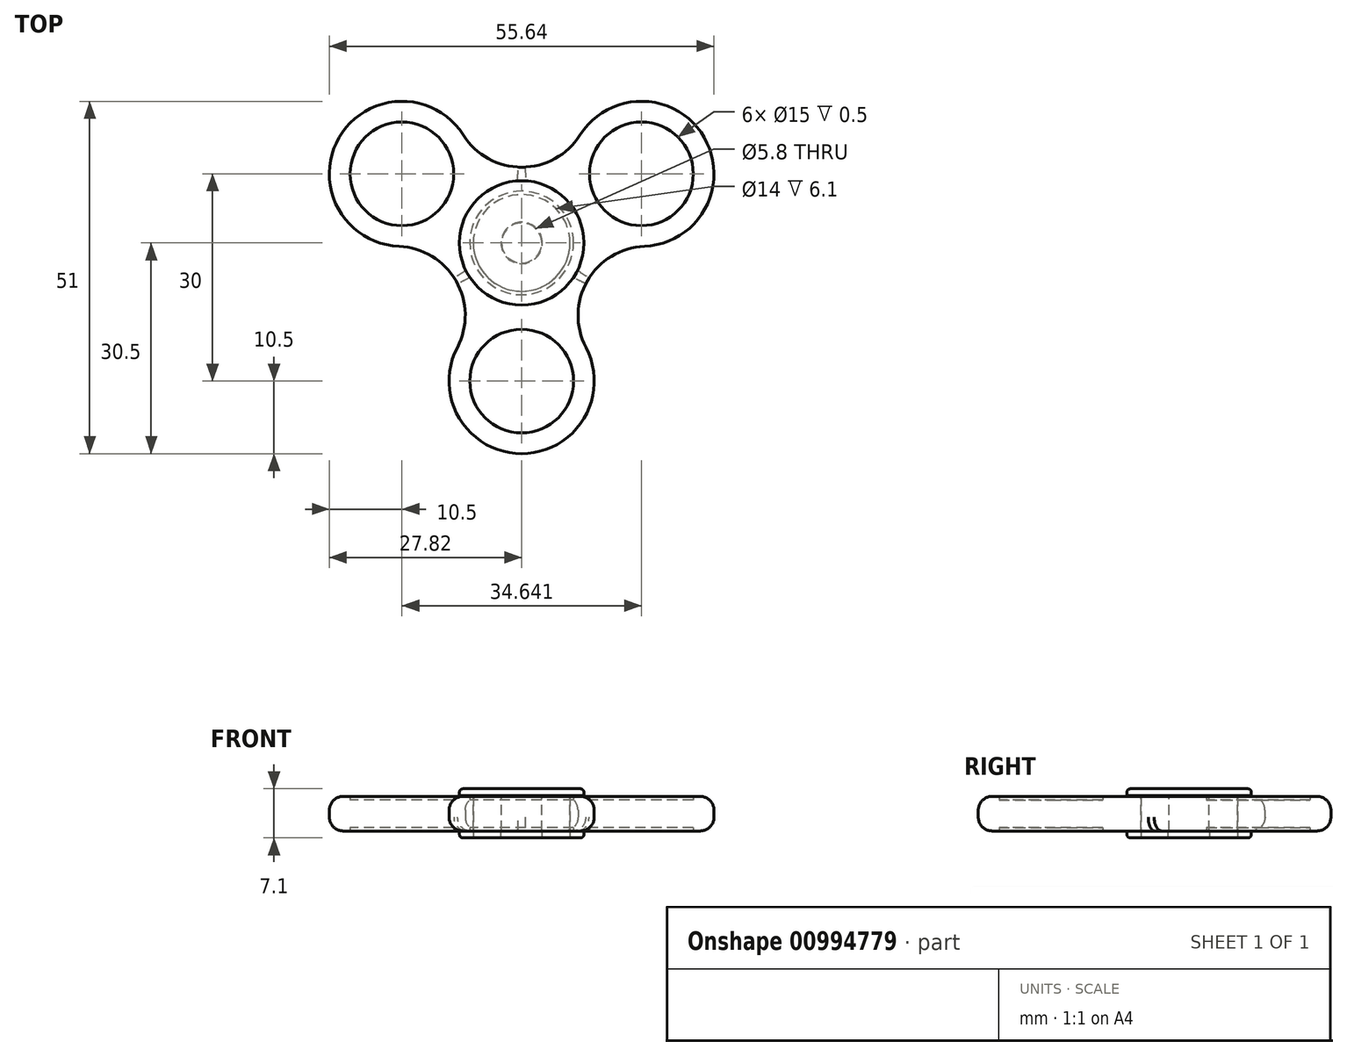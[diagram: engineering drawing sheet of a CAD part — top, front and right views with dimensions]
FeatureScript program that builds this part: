
annotation { "Feature Type Name" : "Feature", "Feature Type Description" : "" }
export const myFeature = defineFeature(function(context is Context, id is Id, definition is map)
    precondition{}
    {
        {
            var Q0;
            Q0=qCreatedBy(makeId("Top.planeOp"),FACE);
            var sketch = newSketch(context, id + "F0", { "sketchPlane" : qUnion([Q0])});
            skCircle(sketch, "E0", {"center": v(0, 0) * mm, "radius": 7.5 * mm});
            skCircle(sketch, "E1", {"center": v(0, -20) * mm, "radius": 7.5 * mm});
            skArc(sketch, "E2", {"start": v(-9.3, -15.13) * mm, "mid": v(0, -30.5) * mm, "end": v(9.3, -15.13) * mm});
            skArc(sketch, "E3.1.0", {"start": v(17.75, -0.5) * mm, "mid": v(26.41, 15.25) * mm, "end": v(8.45, 15.62) * mm});
            skCircle(sketch, "E3.1.1", {"center": v(17.32, 10) * mm, "radius": 7.5 * mm});
            skArc(sketch, "E3.2.0", {"start": v(-8.45, 15.62) * mm, "mid": v(-26.41, 15.25) * mm, "end": v(-17.75, -0.5) * mm});
            skCircle(sketch, "E3.2.1", {"center": v(-17.32, 10) * mm, "radius": 7.5 * mm});
            skArc(sketch, "E4", {"start": v(-9.3, -15.13) * mm, "mid": v(-9.5, -5.48) * mm, "end": v(-17.75, -0.5) * mm});
            skArc(sketch, "E5.1.0", {"start": v(17.75, -0.5) * mm, "mid": v(9.5, -5.48) * mm, "end": v(9.3, -15.13) * mm});
            skArc(sketch, "E5.2.0", {"start": v(-8.45, 15.62) * mm, "mid": v(0, 10.97) * mm, "end": v(8.45, 15.62) * mm});
            skSolve(sketch);
        }
        {
            var Q0;
            Q0=makeQuery(id+"F0.imprint","IMPRINT",FACE,{"disambiguationData":[TD([[makeQuery(id+"F0.imprint","IMPRINT",EDGE,{"derivedFrom":sQuery(id+"F0.wireOp",EDGE,"E0")}),-1.0]])]});
            extrude(context, id + "F1", {"entities" : qUnion([Q0]), "endBound" : BoundingType.SYMMETRIC, "depth" : 5 * mm, "offsetDistance" : 25 * mm});
        }
        {
            var Q0;
            Q0=makeQuery(id+"F0.imprint","IMPRINT",FACE,{"disambiguationData":[TD([[makeQuery(id+"F0.imprint","IMPRINT",EDGE,{"derivedFrom":sQuery(id+"F0.wireOp",EDGE,"E3.1.1")}),1.0]])]});
            var Q1;
            Q1=makeQuery(id+"F0.imprint","IMPRINT",FACE,{"disambiguationData":[TD([[makeQuery(id+"F0.imprint","IMPRINT",EDGE,{"derivedFrom":sQuery(id+"F0.wireOp",EDGE,"E3.2.1")}),1.0]])]});
            var Q2;
            Q2=makeQuery(id+"F0.imprint","IMPRINT",FACE,{"disambiguationData":[TD([[makeQuery(id+"F0.imprint","IMPRINT",EDGE,{"derivedFrom":sQuery(id+"F0.wireOp",EDGE,"E1")}),1.0]])]});
            extrude(context, id + "F2", {"entities" : qUnion([Q0, Q1, Q2]), "operationType" : NewBodyOperationType.ADD, "endBound" : BoundingType.SYMMETRIC, "depth" : 4 * mm, "offsetDistance" : 25 * mm});
        }
        {
            var Q0;
            Q0=makeQuery(id+"F1.opExtrude","CAP_FACE",FACE,{"disambiguationData":[OSD([sQuery(id+"F0.wireOp",EDGE,"E0"),sQuery(id+"F0.wireOp",EDGE,"E1"),sQuery(id+"F0.wireOp",EDGE,"E2"),sQuery(id+"F0.wireOp",EDGE,"E3.1.0"),sQuery(id+"F0.wireOp",EDGE,"E3.1.1"),sQuery(id+"F0.wireOp",EDGE,"E3.2.0"),sQuery(id+"F0.wireOp",EDGE,"E3.2.1"),sQuery(id+"F0.wireOp",EDGE,"E4"),sQuery(id+"F0.wireOp",EDGE,"E5.1.0"),sQuery(id+"F0.wireOp",EDGE,"E5.2.0")])],"isStart":true});
            var sketch = newSketch(context, id + "F3", { "sketchPlane" : qUnion([Q0])});
            skCircle(sketch, "E6.0", {"center": v(0, 0) * mm, "radius": 7 * mm});
            skCircle(sketch, "E7", {"center": v(0, 0) * mm, "radius": 3 * mm});
            skCircle(sketch, "E8.0", {"center": v(0, 0) * mm, "radius": 9 * mm});
            skSolve(sketch);
        }
        {
            var Q0;
            Q0=makeQuery(id+"F3.imprint","IMPRINT",FACE,{"disambiguationData":[TD([[makeQuery(id+"F3.imprint","IMPRINT",EDGE,{"derivedFrom":sQuery(id+"F3.wireOp",EDGE,"E6.0")}),-1.0]])]});
            extrude(context, id + "F4", {"entities" : qUnion([Q0]), "oppositeDirection" : true, "depth" : 5.1 * mm, "offsetDistance" : 25 * mm});
        }
        {
            var Q0;
            Q0 = qSketchRegion(id + "F3", true);
            var Q1;
            Q1=makeQuery(id+"F3.imprint","IMPRINT",FACE,{"disambiguationData":[TD([[makeQuery(id+"F3.imprint","IMPRINT",EDGE,{"derivedFrom":sQuery(id+"F3.wireOp",EDGE,"E6.0")}),-1.0]])]});
            var Q2;
            Q2=makeQuery(id+"F3.imprint","IMPRINT",FACE,{"disambiguationData":[TD([[makeQuery(id+"F3.imprint","IMPRINT",EDGE,{"derivedFrom":sQuery(id+"F3.wireOp",EDGE,"E7")}),1.0]])]});
            var Q3;
            Q3=sQuery(id+"F0.wireOp",EDGE,"E0");
            extrude(context, id + "F5", {"entities" : qUnion([Q0, Q1, Q2]), "operationType" : NewBodyOperationType.ADD, "surfaceOperationType" : NewSurfaceOperationType.ADD, "surfaceEntities" : qUnion([Q3]), "depth" : 1 * mm, "offsetDistance" : 25 * mm});
        }
        {
            var Q0;
            Q0=makeQuery(id+"F4.opExtrude","CAP_FACE",FACE,{"disambiguationData":[OSD([sQuery(id+"F3.wireOp",EDGE,"E6.0"),sQuery(id+"F3.wireOp",EDGE,"E7")])],"isStart":false});
            var sketch = newSketch(context, id + "F6", { "sketchPlane" : qUnion([Q0])});
            skCircle(sketch, "E9.0", {"center": v(0, 0) * mm, "radius": 2.9 * mm});
            skCircle(sketch, "E10.0", {"center": v(0, 0) * mm, "radius": 9 * mm});
            skSolve(sketch);
        }
        {
            var Q0;
            Q0=makeQuery(id+"F6.imprint","IMPRINT",FACE,{"disambiguationData":[TD([[makeQuery(id+"F6.imprint","IMPRINT",EDGE,{"derivedFrom":sQuery(id+"F6.wireOp",EDGE,"E9.0")}),-1.0]])]});
            var Q1;
            Q1=makeQuery(id+"F1.opExtrude","CAP_FACE",FACE,{"disambiguationData":[OSD([sQuery(id+"F0.wireOp",EDGE,"E0"),sQuery(id+"F0.wireOp",EDGE,"E1"),sQuery(id+"F0.wireOp",EDGE,"E2"),sQuery(id+"F0.wireOp",EDGE,"E3.1.0"),sQuery(id+"F0.wireOp",EDGE,"E3.1.1"),sQuery(id+"F0.wireOp",EDGE,"E3.2.0"),sQuery(id+"F0.wireOp",EDGE,"E3.2.1"),sQuery(id+"F0.wireOp",EDGE,"E4"),sQuery(id+"F0.wireOp",EDGE,"E5.1.0"),sQuery(id+"F0.wireOp",EDGE,"E5.2.0")])],"isStart":true});
            extrude(context, id + "F7", {"entities" : qUnion([Q0]), "endBound" : BoundingType.UP_TO_SURFACE, "oppositeDirection" : true, "depth" : 25 * mm, "endBoundEntityFace" : qUnion([Q1]), "offsetDistance" : 25 * mm});
        }
        {
            var Q0;
            Q0=makeQuery(id+"F6.imprint","IMPRINT",FACE,{"disambiguationData":[TD([[makeQuery(id+"F6.imprint","IMPRINT",EDGE,{"derivedFrom":sQuery(id+"F6.wireOp",EDGE,"E10.0")}),1.0]])]});
            var Q1;
            Q1=makeQuery(id+"F6.imprint","IMPRINT",FACE,{"disambiguationData":[TD([[makeQuery(id+"F6.imprint","IMPRINT",EDGE,{"derivedFrom":makeQuery(id+"F4.opExtrude","CAP_EDGE",EDGE,{"disambiguationData":[OSD([sQuery(id+"F3.wireOp",EDGE,"E6.0")])],"isStart":false})}),1.0]])]});
            var Q2;
            Q2=makeQuery(id+"F6.imprint","IMPRINT",FACE,{"disambiguationData":[TD([[makeQuery(id+"F6.imprint","IMPRINT",EDGE,{"derivedFrom":sQuery(id+"F6.wireOp",EDGE,"E9.0")}),-1.0]])]});
            var Q3;
            Q3=makeQuery(id+"F6.imprint","IMPRINT",FACE,{"disambiguationData":[TD([[makeQuery(id+"F6.imprint","IMPRINT",EDGE,{"derivedFrom":sQuery(id+"F6.wireOp",EDGE,"E9.0")}),1.0]])]});
            extrude(context, id + "F8", {"entities" : qUnion([Q0, Q1, Q2, Q3]), "depth" : 1 * mm, "offsetDistance" : 25 * mm});
        }
        {
            var Q0;
            Q0=makeQuery(id+"F1.opExtrude","CAP_EDGE",EDGE,{"disambiguationData":[OSD([sQuery(id+"F0.wireOp",EDGE,"E3.2.0")])],"isStart":false});
            var Q1;
            Q1=makeQuery(id+"F1.opExtrude","CAP_EDGE",EDGE,{"disambiguationData":[OSD([sQuery(id+"F0.wireOp",EDGE,"E3.2.0")])],"isStart":true});
            fillet(context, id + "F9", {"entities" : qUnion([Q0, Q1]), "radius" : 2 * mm, "tangentPropagation" : true, "allowEdgeOverflow" : false});
        }
        {
            var Q0;
            Q0=makeQuery(id+"F8.opExtrude","CAP_FACE",FACE,{"disambiguationData":[OSD([sQuery(id+"F6.wireOp",EDGE,"E10.0")])],"isStart":false});
            var Q1;
            Q1=makeQuery(id+"F5.opExtrude","CAP_EDGE",EDGE,{"disambiguationData":[OSD([sQuery(id+"F3.wireOp",EDGE,"E8.0")])],"isStart":false});
            fillet(context, id + "F10", {"entities" : qUnion([Q0, Q1]), "radius" : 0.5 * mm, "tangentPropagation" : true, "allowEdgeOverflow" : false});
        }
    });
